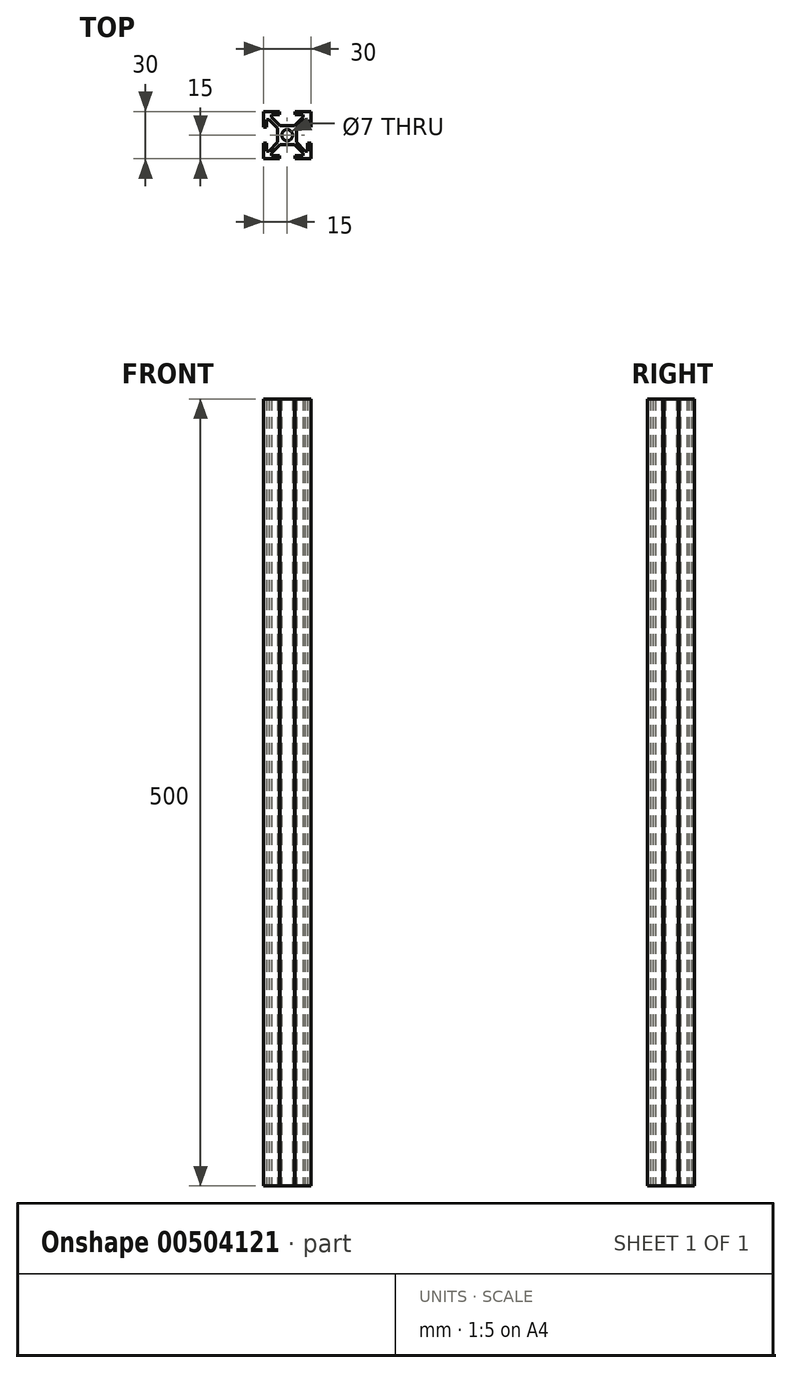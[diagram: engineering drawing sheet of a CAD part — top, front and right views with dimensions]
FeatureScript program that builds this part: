
annotation { "Feature Type Name" : "Feature", "Feature Type Description" : "" }
export const myFeature = defineFeature(function(context is Context, id is Id, definition is map)
    precondition{}
    {
        {
            var Q0;
            Q0=qCreatedBy(makeId("Top.planeOp"),FACE);
            var sketch = newSketch(context, id + "F0", { "sketchPlane" : qUnion([Q0])});
            skCircle(sketch, "E0", {"center": v(0, 0) * mm, "radius": 3.5 * mm});
            skLineSegment(sketch, "E1.bottom", {"start": v(-4.59, 6) * mm, "end": v(4.59, 6) * mm});
            skLineSegment(sketch, "E1.top", {"start": v(-4.59, -6) * mm, "end": v(4.59, -6) * mm});
            skLineSegment(sketch, "E1.left", {"start": v(-6, 4.59) * mm, "end": v(-6, -4.59) * mm});
            skLineSegment(sketch, "E1.right", {"start": v(6, 4.59) * mm, "end": v(6, -4.59) * mm});
            skLineSegment(sketch, "E2", {"start": v(-6, 4.59) * mm, "end": v(-11.41, 10) * mm});
            skLineSegment(sketch, "E3", {"start": v(-4.59, 6) * mm, "end": v(-10, 11.41) * mm});
            skLineSegment(sketch, "E4", {"start": v(-11.41, 10) * mm, "end": v(-13, 10) * mm});
            skLineSegment(sketch, "E5", {"start": v(-13, 10) * mm, "end": v(-13, 5) * mm});
            skLineSegment(sketch, "E6", {"start": v(-13, 5) * mm, "end": v(-15, 5) * mm});
            skLineSegment(sketch, "E7", {"start": v(-15, 5) * mm, "end": v(-15, 15) * mm});
            skLineSegment(sketch, "E8", {"start": v(-15, 15) * mm, "end": v(-5, 15) * mm});
            skLineSegment(sketch, "E9", {"start": v(-5, 15) * mm, "end": v(-5, 13) * mm});
            skLineSegment(sketch, "E10", {"start": v(-5, 13) * mm, "end": v(-10, 13) * mm});
            skLineSegment(sketch, "E11", {"start": v(-10, 13) * mm, "end": v(-10, 11.41) * mm});
            skPoint(sketch, "E12.orphan", {"position": v(-6, 6) * mm});
            skLineSegment(sketch, "E13", {"start": v(0, 0) * mm, "end": v(-5.3, 5.3) * mm, "construction": true});
            skLineSegment(sketch, "E14", {"start": v(-5.3, 5.3) * mm, "end": v(-6, 4.59) * mm, "construction": true});
            skLineSegment(sketch, "E15", {"start": v(-5.3, 5.3) * mm, "end": v(-4.59, 6) * mm, "construction": true});
            skLineSegment(sketch, "E16.2.0", {"start": v(15, 15) * mm, "end": v(15, 5) * mm});
            skLineSegment(sketch, "E16.2.1", {"start": v(5, 15) * mm, "end": v(15, 15) * mm});
            skLineSegment(sketch, "E16.2.2", {"start": v(5, 13) * mm, "end": v(5, 15) * mm});
            skLineSegment(sketch, "E16.2.3", {"start": v(10, 13) * mm, "end": v(5, 13) * mm});
            skLineSegment(sketch, "E16.2.4", {"start": v(10, 11.41) * mm, "end": v(10, 13) * mm});
            skLineSegment(sketch, "E16.2.5", {"start": v(4.59, 6) * mm, "end": v(10, 11.41) * mm});
            skLineSegment(sketch, "E16.2.6", {"start": v(6, 4.59) * mm, "end": v(11.41, 10) * mm});
            skLineSegment(sketch, "E16.2.7", {"start": v(13, 10) * mm, "end": v(11.41, 10) * mm});
            skLineSegment(sketch, "E16.2.8", {"start": v(13, 5) * mm, "end": v(13, 10) * mm});
            skLineSegment(sketch, "E16.2.9", {"start": v(15, 5) * mm, "end": v(13, 5) * mm});
            skLineSegment(sketch, "E16.anchor1", {"start": v(0, 0) * mm, "end": v(-15, 15) * mm, "construction": true});
            skLineSegment(sketch, "E16.anchor2", {"start": v(0, 0) * mm, "end": v(15, 15) * mm, "construction": true});
            skPoint(sketch, "E17.orphan", {"position": v(6, 6) * mm});
            skLineSegment(sketch, "E18.MirrorCS", {"start": v(-13, -5) * mm, "end": v(-15, -5) * mm});
            skLineSegment(sketch, "E19.MirrorCS", {"start": v(-15, -5) * mm, "end": v(-15, -15) * mm});
            skLineSegment(sketch, "E20.MirrorCS", {"start": v(-13, -10) * mm, "end": v(-13, -5) * mm});
            skLineSegment(sketch, "E21.MirrorCS", {"start": v(-11.41, -10) * mm, "end": v(-13, -10) * mm});
            skLineSegment(sketch, "E22.MirrorCS", {"start": v(-6, -4.59) * mm, "end": v(-11.41, -10) * mm});
            skLineSegment(sketch, "E23.MirrorCS", {"start": v(-4.59, -6) * mm, "end": v(-10, -11.41) * mm});
            skLineSegment(sketch, "E24.MirrorCS", {"start": v(-5, -13) * mm, "end": v(-10, -13) * mm});
            skLineSegment(sketch, "E25.MirrorCS", {"start": v(-10, -13) * mm, "end": v(-10, -11.41) * mm});
            skLineSegment(sketch, "E26.MirrorCS", {"start": v(-5, -15) * mm, "end": v(-5, -13) * mm});
            skLineSegment(sketch, "E27.MirrorCS", {"start": v(-15, -15) * mm, "end": v(-5, -15) * mm});
            skLineSegment(sketch, "E28.MirrorCS", {"start": v(5, -13) * mm, "end": v(5, -15) * mm});
            skLineSegment(sketch, "E29.MirrorCS", {"start": v(5, -15) * mm, "end": v(15, -15) * mm});
            skLineSegment(sketch, "E30.MirrorCS", {"start": v(15, -15) * mm, "end": v(15, -5) * mm});
            skLineSegment(sketch, "E31.MirrorCS", {"start": v(15, -5) * mm, "end": v(13, -5) * mm});
            skLineSegment(sketch, "E32.MirrorCS", {"start": v(13, -5) * mm, "end": v(13, -10) * mm});
            skLineSegment(sketch, "E33.MirrorCS", {"start": v(13, -10) * mm, "end": v(11.41, -10) * mm});
            skLineSegment(sketch, "E34.MirrorCS", {"start": v(6, -4.59) * mm, "end": v(11.41, -10) * mm});
            skLineSegment(sketch, "E35.MirrorCS", {"start": v(4.59, -6) * mm, "end": v(10, -11.41) * mm});
            skLineSegment(sketch, "E36.MirrorCS", {"start": v(10, -13) * mm, "end": v(5, -13) * mm});
            skLineSegment(sketch, "E37.MirrorCS", {"start": v(10, -11.41) * mm, "end": v(10, -13) * mm});
            skPoint(sketch, "E38.orphan", {"position": v(-6, -6) * mm});
            skPoint(sketch, "E39.orphan", {"position": v(6, -6) * mm});
            skSolve(sketch);
        }
        {
            var Q0;
            Q0 = qSketchRegion(id + "F0", true);
            extrude(context, id + "F1", {"entities" : qUnion([Q0]), "depth" : 500 * mm});
        }
    });
